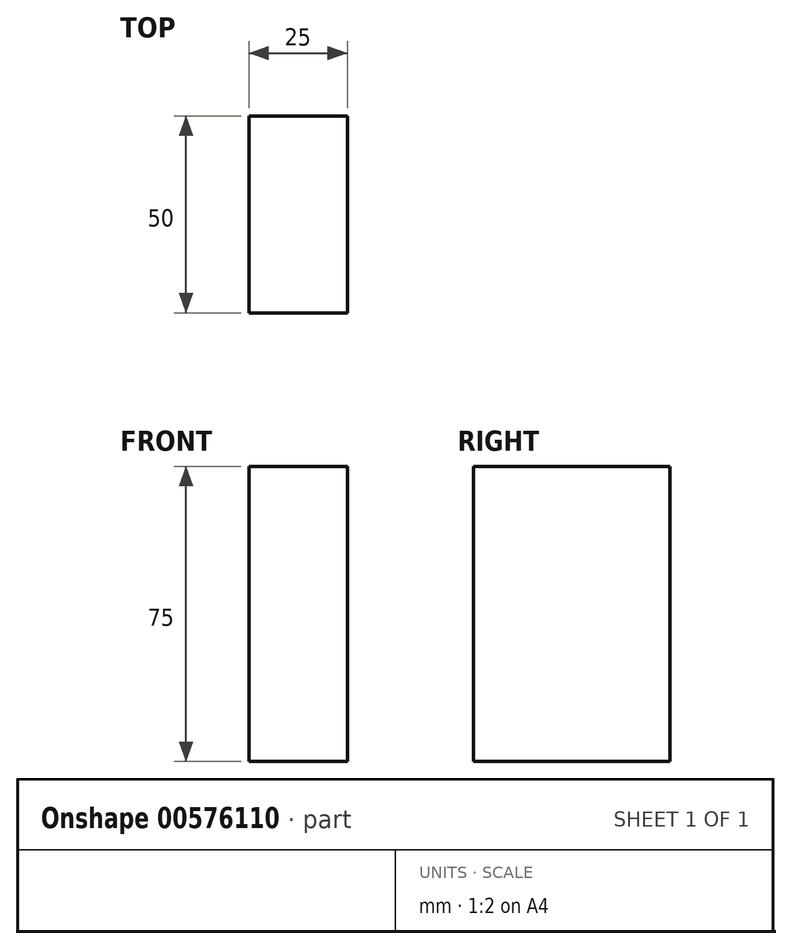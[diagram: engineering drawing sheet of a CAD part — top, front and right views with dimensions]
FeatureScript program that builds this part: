
annotation { "Feature Type Name" : "Feature", "Feature Type Description" : "" }
export const myFeature = defineFeature(function(context is Context, id is Id, definition is map)
    precondition{}
    {
        {
            var Q0;
            Q0=qCreatedBy(makeId("Top.planeOp"),FACE);
            var sketch = newSketch(context, id + "F0", { "sketchPlane" : qUnion([Q0])});
            skLineSegment(sketch, "E0.bottom", {"start": v(0, 0) * mm, "end": v(25, 0) * mm});
            skLineSegment(sketch, "E0.top", {"start": v(0, -50) * mm, "end": v(25, -50) * mm});
            skLineSegment(sketch, "E0.left", {"start": v(0, 0) * mm, "end": v(0, -50) * mm});
            skLineSegment(sketch, "E0.right", {"start": v(25, 0) * mm, "end": v(25, -50) * mm});
            skSolve(sketch);
        }
        {
            var Q0;
            Q0 = qSketchRegion(id + "F0", true);
            extrude(context, id + "F1", {"entities" : qUnion([Q0]), "depth" : 75 * mm, "offsetDistance" : 25 * mm});
        }
    });
